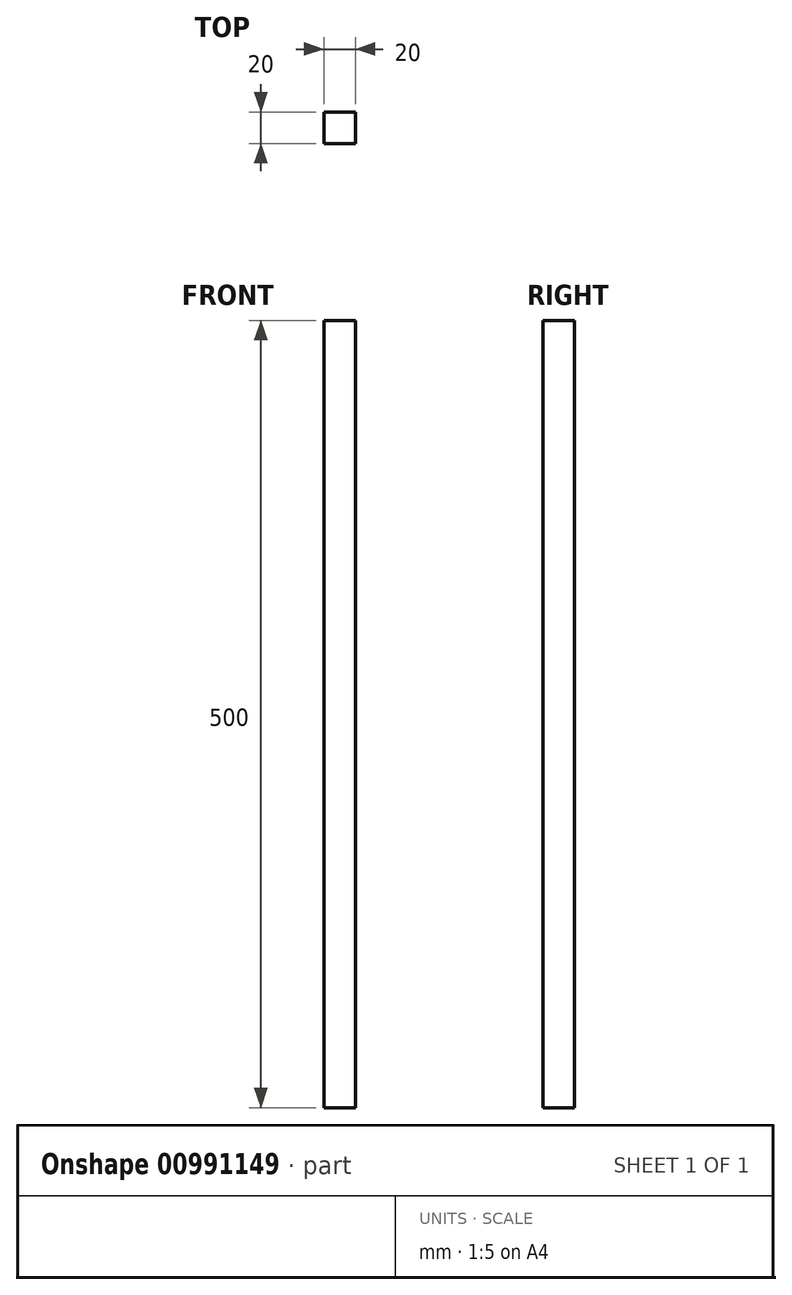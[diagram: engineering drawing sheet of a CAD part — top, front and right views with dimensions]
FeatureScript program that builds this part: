
annotation { "Feature Type Name" : "Feature", "Feature Type Description" : "" }
export const myFeature = defineFeature(function(context is Context, id is Id, definition is map)
    precondition{}
    {
        {
            var Q0;
            Q0=qCreatedBy(makeId("Top.planeOp"),FACE);
            var sketch = newSketch(context, id + "F0", { "sketchPlane" : qUnion([Q0])});
            skLineSegment(sketch, "E0.bottom", {"start": v(0, 0) * mm, "end": v(20, 0) * mm});
            skLineSegment(sketch, "E0.top", {"start": v(0, 20) * mm, "end": v(20, 20) * mm});
            skLineSegment(sketch, "E0.left", {"start": v(0, 0) * mm, "end": v(0, 20) * mm});
            skLineSegment(sketch, "E0.right", {"start": v(20, 0) * mm, "end": v(20, 20) * mm});
            skSolve(sketch);
        }
        {
            var Q0;
            Q0=makeQuery(id+"F0.imprint","IMPRINT",FACE,{"disambiguationData":[TD([[makeQuery(id+"F0.imprint","IMPRINT",EDGE,{"derivedFrom":sQuery(id+"F0.wireOp",EDGE,"E0.bottom")}),1.0]])]});
            extrude(context, id + "F1", {"entities" : qUnion([Q0]), "depth" : 500 * mm, "offsetDistance" : 25 * mm});
        }
    });
